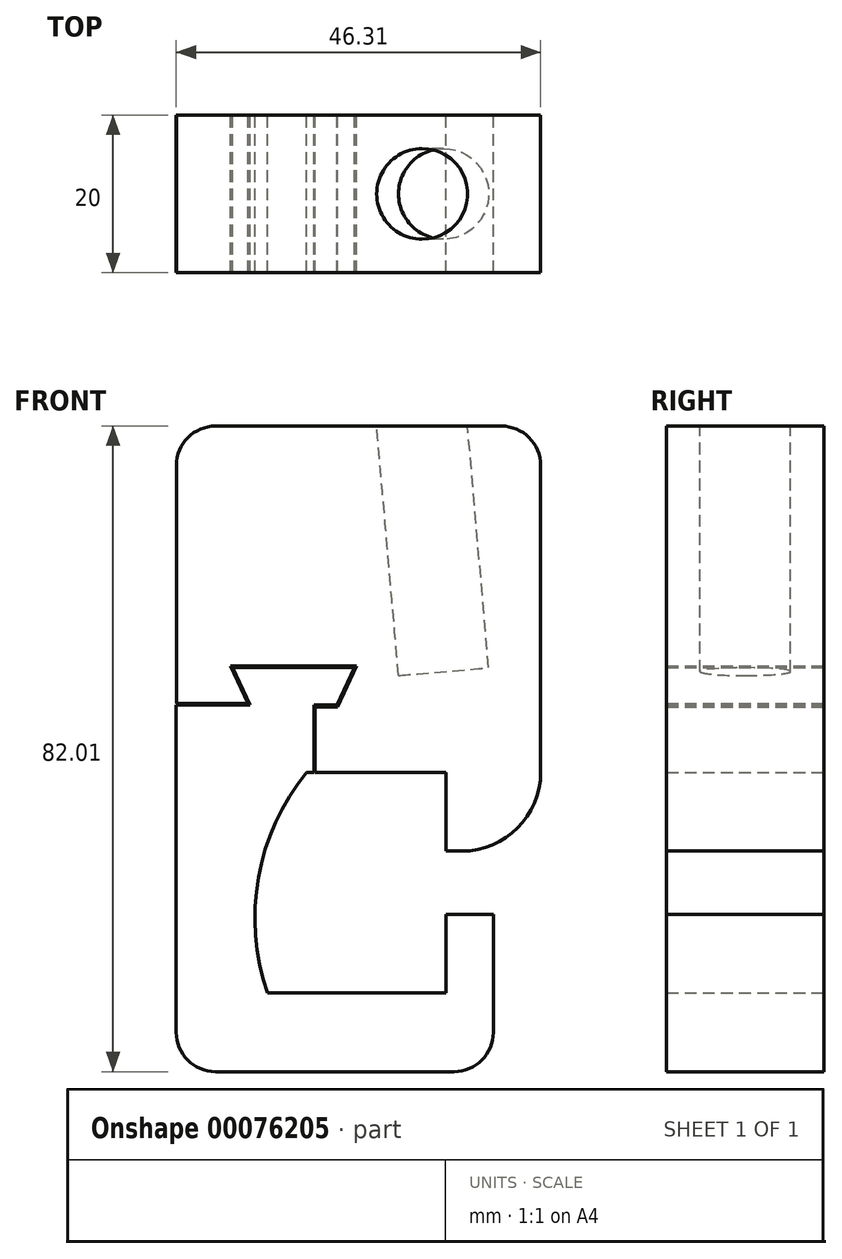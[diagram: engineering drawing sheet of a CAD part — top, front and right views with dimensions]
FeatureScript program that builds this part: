
annotation { "Feature Type Name" : "Feature", "Feature Type Description" : "" }
export const myFeature = defineFeature(function(context is Context, id is Id, definition is map)
    precondition{}
    {
        {
            var Q0;
            Q0=qCreatedBy(makeId("Front.planeOp"),FACE);
            var sketch = newSketch(context, id + "F0", { "sketchPlane" : qUnion([Q0])});
            skLineSegment(sketch, "E0", {"start": v(-27.09, 22.4) * mm, "end": v(-27.09, -19.15) * mm});
            skLineSegment(sketch, "E1", {"start": v(-22.09, -24.15) * mm, "end": v(8.21, -24.15) * mm});
            skLineSegment(sketch, "E2", {"start": v(13.21, -19.15) * mm, "end": v(13.21, -4.15) * mm});
            skLineSegment(sketch, "E3", {"start": v(13.21, -4.15) * mm, "end": v(7.21, -4.15) * mm});
            skLineSegment(sketch, "E4", {"start": v(7.21, -4.15) * mm, "end": v(7.21, -14.15) * mm});
            skLineSegment(sketch, "E5", {"start": v(7.21, -14.15) * mm, "end": v(-15.49, -14.15) * mm});
            skLineSegment(sketch, "E6", {"start": v(-9.6, 13.85) * mm, "end": v(-10.5, 13.85) * mm});
            skArc(sketch, "E7", {"start": v(-10.5, 13.85) * mm, "mid": v(-16.63, 0.5) * mm, "end": v(-15.49, -14.15) * mm});
            skLineSegment(sketch, "E8", {"start": v(-9.6, 13.85) * mm, "end": v(-9.6, 22.4) * mm});
            skLineSegment(sketch, "E9", {"start": v(-17.67, 22.4) * mm, "end": v(-19.91, 27.2) * mm});
            skLineSegment(sketch, "E10", {"start": v(-19.91, 27.2) * mm, "end": v(-4.41, 27.2) * mm});
            skLineSegment(sketch, "E11", {"start": v(-17.67, 22.4) * mm, "end": v(-27.09, 22.4) * mm});
            skPoint(sketch, "E12.visualSharp", {"position": v(-27.09, -24.15) * mm});
            skArc(sketch, "E12.filletArc", {"start": v(-27.09, -19.15) * mm, "mid": v(-25.62, -22.68) * mm, "end": v(-22.09, -24.15) * mm});
            skPoint(sketch, "E13.visualSharp", {"position": v(13.21, -24.15) * mm});
            skArc(sketch, "E13.filletArc", {"start": v(8.21, -24.15) * mm, "mid": v(11.75, -22.68) * mm, "end": v(13.21, -19.15) * mm});
            skLineSegment(sketch, "E14", {"start": v(-9.6, 22.4) * mm, "end": v(-6.65, 22.4) * mm});
            skLineSegment(sketch, "E15", {"start": v(-4.41, 27.2) * mm, "end": v(-6.65, 22.4) * mm});
            skSolve(sketch);
        }
        {
            var Q0;
            Q0=qCreatedBy(makeId("Front.planeOp"),FACE);
            var sketch = newSketch(context, id + "F1", { "sketchPlane" : qUnion([Q0])});
            skLineSegment(sketch, "E16", {"start": v(7.22, 13.86) * mm, "end": v(7.22, 3.86) * mm});
            skLineSegment(sketch, "E17", {"start": v(7.22, 3.86) * mm, "end": v(19.22, 3.86) * mm});
            skLineSegment(sketch, "E18", {"start": v(7.22, 13.86) * mm, "end": v(-9.43, 13.86) * mm});
            skLineSegment(sketch, "E19", {"start": v(19.22, 3.86) * mm, "end": v(19.22, 57.86) * mm});
            skLineSegment(sketch, "E20", {"start": v(19.22, 57.86) * mm, "end": v(-27.07, 57.86) * mm});
            skLineSegment(sketch, "E21", {"start": v(-27.07, 57.86) * mm, "end": v(-27.07, 22.65) * mm});
            skLineSegment(sketch, "E22", {"start": v(-17.94, 22.65) * mm, "end": v(-20.15, 27.4) * mm});
            skLineSegment(sketch, "E23", {"start": v(-20.15, 27.4) * mm, "end": v(-4.15, 27.4) * mm});
            skLineSegment(sketch, "E24", {"start": v(-27.07, 22.65) * mm, "end": v(-17.94, 22.65) * mm});
            skLineSegment(sketch, "E25", {"start": v(-5.97, 22.5) * mm, "end": v(-28.83, 22.5) * mm, "construction": true});
            skLineSegment(sketch, "E26", {"start": v(-9.43, 22.19) * mm, "end": v(-9.43, 13.86) * mm});
            skLineSegment(sketch, "E27", {"start": v(-9.43, 22.19) * mm, "end": v(-4.15, 22.19) * mm});
            skLineSegment(sketch, "E28", {"start": v(-4.15, 27.4) * mm, "end": v(-6.58, 22.19) * mm});
            skSolve(sketch);
        }
        {
            var Q0;
            Q0=makeQuery(id+"F0.imprint","IMPRINT",FACE,{"disambiguationData":[TD([[makeQuery(id+"F0.imprint","IMPRINT",EDGE,{"derivedFrom":sQuery(id+"F0.wireOp",EDGE,"E0")}),1.0]])]});
            extrude(context, id + "F2", {"entities" : qUnion([Q0]), "depth" : 20 * mm});
        }
        {
            var Q0;
            Q0 = qSketchRegion(id + "F1", true);
            extrude(context, id + "F3", {"entities" : qUnion([Q0]), "operationType" : NewBodyOperationType.ADD, "depth" : 20 * mm});
        }
        {
            var Q0;
            Q0=makeQuery(id+"F3.opExtrude","SWEPT_EDGE",EDGE,{"disambiguationData":[OSD([sQuery(id+"F1.wireOp",EDGE,"E19"),sQuery(id+"F1.wireOp",EDGE,"E20")])]});
            cPlane(context, id + "F4", {"entities" : qUnion([Q0]), "cplaneType" : CPlaneType.LINE_ANGLE, "offset" : 25 * mm, "angle" : 175 * degree, "width" : 150 * mm, "height" : 150 * mm});
        }
        {
            var Q0;
            Q0=qCreatedBy(id+"F4.planeOp",FACE);
            cPlane(context, id + "F5", {"entities" : qUnion([Q0]), "cplaneType" : CPlaneType.OFFSET, "offset" : 15 * mm, "oppositeDirection" : true, "width" : 150 * mm, "height" : 150 * mm});
        }
        {
            var Q0;
            Q0=qCreatedBy(id+"F5.planeOp",FACE);
            var sketch = newSketch(context, id + "F6", { "sketchPlane" : qUnion([Q0])});
            skCircle(sketch, "E29", {"center": v(9.19, 10) * mm, "radius": 5.75 * mm});
            skSolve(sketch);
        }
        {
            var Q0;
            Q0=makeQuery(id+"F6.imprint","IMPRINT",FACE,{"disambiguationData":[TD([[makeQuery(id+"F6.imprint","IMPRINT",EDGE,{"derivedFrom":sQuery(id+"F6.wireOp",EDGE,"E29")}),1.0]])]});
            extrude(context, id + "F7", {"entities" : qUnion([Q0]), "operationType" : NewBodyOperationType.REMOVE, "depth" : 45 * mm});
        }
        {
            var Q0;
            Q0=makeQuery(id+"F3.opExtrude","SWEPT_EDGE",EDGE,{"disambiguationData":[OSD([sQuery(id+"F1.wireOp",EDGE,"E20"),sQuery(id+"F1.wireOp",EDGE,"E21")])]});
            var Q1;
            Q1=makeQuery(id+"F3.opExtrude","SWEPT_EDGE",EDGE,{"disambiguationData":[OSD([sQuery(id+"F1.wireOp",EDGE,"E19"),sQuery(id+"F1.wireOp",EDGE,"E20")])]});
            fillet(context, id + "F8", {"entities" : qUnion([Q0, Q1]), "radius" : 5 * mm, "tangentPropagation" : true, "allowEdgeOverflow" : false});
        }
        {
            var Q0;
            Q0=makeQuery(id+"F3.opExtrude","SWEPT_EDGE",EDGE,{"disambiguationData":[OSD([sQuery(id+"F1.wireOp",EDGE,"E17"),sQuery(id+"F1.wireOp",EDGE,"E19")])]});
            fillet(context, id + "F9", {"entities" : qUnion([Q0]), "tangentPropagation" : true, "radius" : 10 * mm, "defaultsChanged" : true, "vertexSettings" : [], "allowEdgeOverflow" : false});
        }
    });
